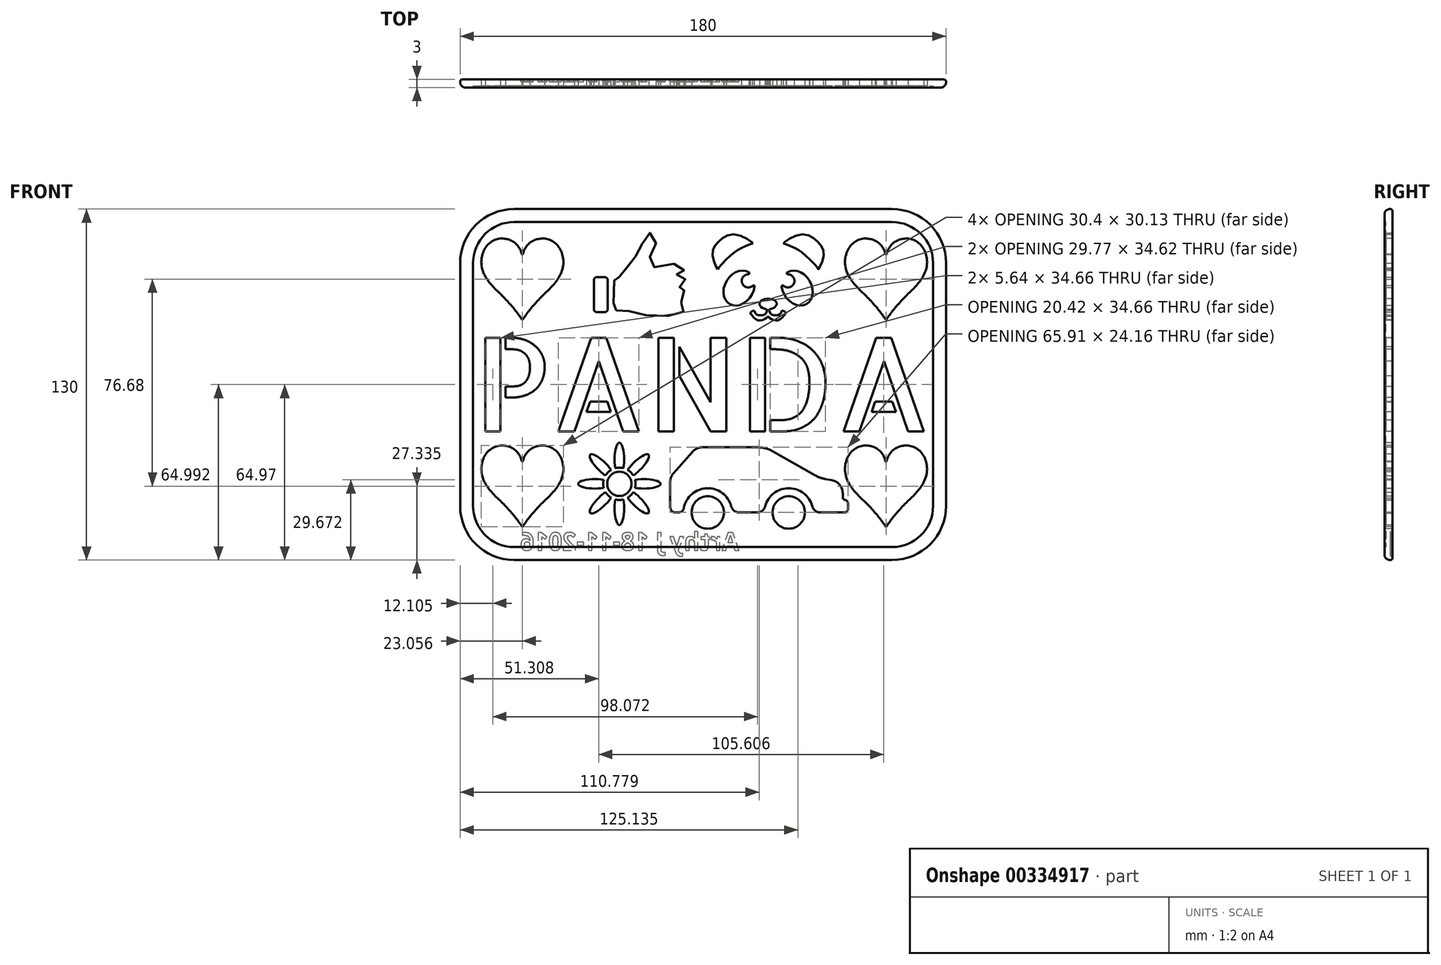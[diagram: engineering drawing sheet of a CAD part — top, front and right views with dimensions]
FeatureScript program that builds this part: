
annotation { "Feature Type Name" : "Feature", "Feature Type Description" : "" }
export const myFeature = defineFeature(function(context is Context, id is Id, definition is map)
    precondition{}
    {
        {
            var Q0;
            Q0=qCreatedBy(makeId("Front.planeOp"),FACE);
            var sketch = newSketch(context, id + "F0", { "sketchPlane" : qUnion([Q0])});
            skLineSegment(sketch, "E0.bottom", {"start": v(-90, 65) * mm, "end": v(90, 65) * mm});
            skLineSegment(sketch, "E0.top", {"start": v(-90, -65) * mm, "end": v(90, -65) * mm});
            skLineSegment(sketch, "E0.left", {"start": v(-90, 65) * mm, "end": v(-90, -65) * mm});
            skLineSegment(sketch, "E0.right", {"start": v(90, 65) * mm, "end": v(90, -65) * mm});
            skSolve(sketch);
        }
        {
            var Q0;
            Q0=qSketchRegion(id+"F0",true);
            extrude(context, id + "F1", {"entities" : qUnion([Q0]), "depth" : 3 * mm});
        }
        {
            var Q0;
            Q0=makeQuery(id+"F1.opExtrude","CAP_FACE",FACE,{"disambiguationData":[OSD([sQuery(id+"F0.wireOp",EDGE,"E0.bottom"),sQuery(id+"F0.wireOp",EDGE,"E0.top"),sQuery(id+"F0.wireOp",EDGE,"E0.left"),sQuery(id+"F0.wireOp",EDGE,"E0.right")])],"isStart":false});
            var sketch = newSketch(context, id + "F2", { "sketchPlane" : qUnion([Q0])});
            skText(sketch, "E1", { "text": "PANDA", "fontName": "AllertaStencil-Regular.ttf"});
            skText(sketch, "E2", { "text": "♥", "fontName": "NotoSansCJKjp-Regular.otf"});
            skText(sketch, "E3", { "text": "♥", "fontName": "NotoSansCJKjp-Regular.otf"});
            skText(sketch, "E4", { "text": "♥", "fontName": "NotoSansCJKjp-Regular.otf"});
            skText(sketch, "E5", { "text": "♥", "fontName": "NotoSansCJKjp-Regular.otf"});
            const initialGuessF2  = {"E1": [-0.085, -0.01734, 1, 0, 0.03468], "E2": [0.04972, 0.02534, 1, 0, 0.026], "E3": [-0.085, 0.02534, 1, 0, 0.026], "E4": [-0.085, -0.05134, 1, 0, 0.026], "E5": [0.04972, -0.05134, 1, 0, 0.026]};
            skSetInitialGuess(sketch, initialGuessF2);
            skSolve(sketch);
        }
        {
            var Q0;
            Q0=qSketchRegion(id+"F2",true);
            extrude(context, id + "F3", {"entities" : qUnion([Q0]), "operationType" : NewBodyOperationType.REMOVE, "endBound" : BoundingType.THROUGH_ALL, "oppositeDirection" : true, "depth" : 25 * mm});
        }
        {
            var Q0;
            Q0=makeQuery(id+"F1.opExtrude","SWEPT_EDGE",EDGE,{"disambiguationData":[OSD([sQuery(id+"F0.wireOp",EDGE,"E0.top"),sQuery(id+"F0.wireOp",EDGE,"E0.right")])]});
            var Q1;
            Q1=makeQuery(id+"F1.opExtrude","SWEPT_EDGE",EDGE,{"disambiguationData":[OSD([sQuery(id+"F0.wireOp",EDGE,"E0.bottom"),sQuery(id+"F0.wireOp",EDGE,"E0.right")])]});
            var Q2;
            Q2=makeQuery(id+"F1.opExtrude","SWEPT_EDGE",EDGE,{"disambiguationData":[OSD([sQuery(id+"F0.wireOp",EDGE,"E0.top"),sQuery(id+"F0.wireOp",EDGE,"E0.left")])]});
            var Q3;
            Q3=makeQuery(id+"F1.opExtrude","SWEPT_EDGE",EDGE,{"disambiguationData":[OSD([sQuery(id+"F0.wireOp",EDGE,"E0.bottom"),sQuery(id+"F0.wireOp",EDGE,"E0.left")])]});
            fillet(context, id + "F4", {"entities" : qUnion([Q0, Q1, Q2, Q3]), "radius" : 20 * mm, "tangentPropagation" : true, "allowEdgeOverflow" : false});
        }
        {
            var Q0;
            Q0=makeQuery(id+"F1.opExtrude","CAP_FACE",FACE,{"disambiguationData":[OSD([sQuery(id+"F0.wireOp",EDGE,"E0.bottom"),sQuery(id+"F0.wireOp",EDGE,"E0.top"),sQuery(id+"F0.wireOp",EDGE,"E0.left"),sQuery(id+"F0.wireOp",EDGE,"E0.right")])],"isStart":false});
            var sketch = newSketch(context, id + "F5", { "sketchPlane" : qUnion([Q0])});
            skLineSegment(sketch, "E6.0", {"start": v(-70, -60.2) * mm, "end": v(70, -60.2) * mm});
            skArc(sketch, "E6.1", {"start": v(-85.2, -45) * mm, "mid": v(-80.75, -55.75) * mm, "end": v(-70, -60.2) * mm});
            skArc(sketch, "E6.2", {"start": v(70, -60.2) * mm, "mid": v(80.75, -55.75) * mm, "end": v(85.2, -45) * mm});
            skLineSegment(sketch, "E6.3", {"start": v(-85.2, 45) * mm, "end": v(-85.2, -45) * mm});
            skLineSegment(sketch, "E6.4", {"start": v(85.2, -45) * mm, "end": v(85.2, 45) * mm});
            skArc(sketch, "E6.5", {"start": v(85.2, 45) * mm, "mid": v(80.75, 55.75) * mm, "end": v(70, 60.2) * mm});
            skLineSegment(sketch, "E6.6", {"start": v(70, 60.2) * mm, "end": v(-70, 60.2) * mm});
            skArc(sketch, "E6.7", {"start": v(-70, 60.2) * mm, "mid": v(-80.75, 55.75) * mm, "end": v(-85.2, 45) * mm});
            skSolve(sketch);
        }
        {
            var Q0;
            Q0=qSketchRegion(id+"F5",true);
            extrude(context, id + "F6", {"entities" : qUnion([Q0]), "operationType" : NewBodyOperationType.REMOVE, "oppositeDirection" : true, "depth" : 0.6 * mm});
        }
        {
            var Q0;
            Q0=makeQuery(id+"F6.boolean.opBoolean","COPY",FACE,{"derivedFrom":makeQuery(id+"F6.opExtrude","CAP_FACE",FACE,{"disambiguationData":[OSD([sQuery(id+"F5.wireOp",EDGE,"E6.0"),sQuery(id+"F5.wireOp",EDGE,"E6.1"),sQuery(id+"F5.wireOp",EDGE,"E6.2"),sQuery(id+"F5.wireOp",EDGE,"E6.3"),sQuery(id+"F5.wireOp",EDGE,"E6.4"),sQuery(id+"F5.wireOp",EDGE,"E6.5"),sQuery(id+"F5.wireOp",EDGE,"E6.6"),sQuery(id+"F5.wireOp",EDGE,"E6.7")])],"isStart":false})});
            var sketch = newSketch(context, id + "F7", { "sketchPlane" : qUnion([Q0])});
            skLineSegment(sketch, "E7", {"start": v(13.35, -47.4) * mm, "end": v(20.11, -47.4) * mm, "construction": true});
            skCircle(sketch, "E8", {"center": v(1.73, -47.4) * mm, "radius": 6 * mm});
            skCircle(sketch, "E9", {"center": v(31.73, -47.4) * mm, "radius": 6 * mm});
            skArc(sketch, "E10", {"start": v(10.45, -45.16) * mm, "mid": v(1.42, -38.41) * mm, "end": v(-7.12, -45.77) * mm});
            skArc(sketch, "E11", {"start": v(40.45, -45.16) * mm, "mid": v(31.73, -38.4) * mm, "end": v(23.02, -45.16) * mm});
            skLineSegment(sketch, "E12", {"start": v(21.73, -47.4) * mm, "end": v(11.73, -47.4) * mm});
            skLineSegment(sketch, "E13", {"start": v(-9.08, -47.4) * mm, "end": v(-10.17, -47.4) * mm});
            skLineSegment(sketch, "E14", {"start": v(-12.17, -45.4) * mm, "end": v(-12.17, -36.14) * mm});
            skLineSegment(sketch, "E15", {"start": v(-10.93, -32.84) * mm, "end": v(-4, -24.95) * mm});
            skLineSegment(sketch, "E16", {"start": v(-0.25, -23.25) * mm, "end": v(20.03, -23.25) * mm});
            skLineSegment(sketch, "E17", {"start": v(25.99, -24.83) * mm, "end": v(41.29, -33.57) * mm});
            skLineSegment(sketch, "E18", {"start": v(45.19, -34.98) * mm, "end": v(47.59, -35.4) * mm});
            skLineSegment(sketch, "E19", {"start": v(51.73, -40.32) * mm, "end": v(51.73, -41.75) * mm});
            skLineSegment(sketch, "E20", {"start": v(52.4, -42.75) * mm, "end": v(52.73, -42.75) * mm});
            skLineSegment(sketch, "E21", {"start": v(53.73, -44.07) * mm, "end": v(53.73, -46.09) * mm});
            skLineSegment(sketch, "E22", {"start": v(52.4, -47.4) * mm, "end": v(43.35, -47.4) * mm});
            skPoint(sketch, "E23.visualSharp", {"position": v(-12.17, -34.25) * mm});
            skArc(sketch, "E23.filletArc", {"start": v(-10.93, -32.84) * mm, "mid": v(-11.85, -34.37) * mm, "end": v(-12.17, -36.14) * mm});
            skPoint(sketch, "E24.visualSharp", {"position": v(-2.51, -23.25) * mm});
            skArc(sketch, "E24.filletArc", {"start": v(-0.25, -23.25) * mm, "mid": v(-2.31, -23.7) * mm, "end": v(-4, -24.95) * mm});
            skPoint(sketch, "E25.visualSharp", {"position": v(23.22, -23.25) * mm});
            skArc(sketch, "E25.filletArc", {"start": v(25.99, -24.83) * mm, "mid": v(23.11, -23.65) * mm, "end": v(20.03, -23.25) * mm});
            skPoint(sketch, "E26.visualSharp", {"position": v(43.11, -34.61) * mm});
            skArc(sketch, "E26.filletArc", {"start": v(41.29, -33.57) * mm, "mid": v(43.18, -34.44) * mm, "end": v(45.19, -34.98) * mm});
            skPoint(sketch, "E27.visualSharp", {"position": v(51.73, -36.11) * mm});
            skArc(sketch, "E27.filletArc", {"start": v(51.73, -40.32) * mm, "mid": v(50.56, -37.1) * mm, "end": v(47.59, -35.4) * mm});
            skPoint(sketch, "E28.visualSharp", {"position": v(53.73, -42.75) * mm});
            skArc(sketch, "E28.filletArc", {"start": v(53.73, -44.07) * mm, "mid": v(53.34, -43.13) * mm, "end": v(52.4, -42.75) * mm});
            skPoint(sketch, "E29.visualSharp", {"position": v(53.73, -47.4) * mm});
            skArc(sketch, "E29.filletArc", {"start": v(52.4, -47.4) * mm, "mid": v(53.34, -47.02) * mm, "end": v(53.73, -46.09) * mm});
            skPoint(sketch, "E30.visualSharp", {"position": v(51.73, -42.75) * mm});
            skArc(sketch, "E30.filletArc", {"start": v(51.73, -41.75) * mm, "mid": v(52.02, -42.45) * mm, "end": v(52.73, -42.75) * mm});
            skPoint(sketch, "E31.newPointA", {"position": v(10.73, -47.4) * mm});
            skPoint(sketch, "E31.newPointB", {"position": v(-7.31, -47.4) * mm});
            skArc(sketch, "E31.filletArc", {"start": v(10.45, -45.16) * mm, "mid": v(11.51, -46.78) * mm, "end": v(13.35, -47.4) * mm});
            skArc(sketch, "E32.filletArc", {"start": v(20.11, -47.4) * mm, "mid": v(21.95, -46.78) * mm, "end": v(23.02, -45.16) * mm});
            skPoint(sketch, "E33.visualSharp", {"position": v(40.73, -47.4) * mm});
            skArc(sketch, "E33.filletArc", {"start": v(40.45, -45.16) * mm, "mid": v(41.51, -46.78) * mm, "end": v(43.35, -47.4) * mm});
            skPoint(sketch, "E34.visualSharp", {"position": v(-7.27, -47.4) * mm});
            skArc(sketch, "E34.filletArc", {"start": v(-9.08, -47.4) * mm, "mid": v(-7.8, -46.95) * mm, "end": v(-7.12, -45.77) * mm});
            skPoint(sketch, "E35.visualSharp", {"position": v(-12.17, -47.4) * mm});
            skArc(sketch, "E35.filletArc", {"start": v(-12.17, -45.4) * mm, "mid": v(-11.59, -46.82) * mm, "end": v(-10.17, -47.4) * mm});
            skSolve(sketch);
        }
        {
            var Q0;
            Q0=qSketchRegion(id+"F7",true);
            extrude(context, id + "F8", {"entities" : qUnion([Q0]), "operationType" : NewBodyOperationType.REMOVE, "endBound" : BoundingType.THROUGH_ALL, "oppositeDirection" : true, "depth" : 25 * mm});
        }
        {
            var Q0;
            Q0=qCreatedBy(makeId("Front.planeOp"),FACE);
            var sketch = newSketch(context, id + "F9", { "sketchPlane" : qUnion([Q0])});
            skFitSpline(sketch, "E36", {"points": [v(-32.1, 27.5) * mm, v(-32.86, 27.86) * mm, v(-33.14, 28.78) * mm, v(-32.88, 38.83) * mm, v(-32.72, 39) * mm, v(-31.87, 39.13) * mm, v(-29.86, 41.3) * mm, v(-28.11, 43.43) * mm, v(-24.92, 47.62) * mm, v(-22.64, 51.97) * mm, v(-20.28, 56.13) * mm, v(-17.45, 54.28) * mm, v(-18.66, 49.2) * mm, v(-19.93, 45.57) * mm, v(-17.05, 43.26) * mm, v(-8.14, 44.72) * mm, v(-7.33, 41.85) * mm, v(-9.69, 41.12) * mm, v(-9.64, 40.61) * mm, v(-7.18, 40.03) * mm, v(-7.04, 36.55) * mm, v(-8.92, 36.07) * mm, v(-8.92, 35.64) * mm, v(-7.07, 34.9) * mm, v(-7.12, 31.5) * mm, v(-9.05, 30.54) * mm, v(-9.26, 30.08) * mm, v(-7.05, 29.74) * mm, v(-6.93, 27.4) * mm, v(-11.96, 25.52) * mm, v(-22.62, 25.9) * mm, v(-28.82, 27.45) * mm, v(-32.1, 27.5) * mm]});
            skLineSegment(sketch, "E37.bottom", {"start": v(-36.34, 39.73) * mm, "end": v(-39.43, 39.73) * mm});
            skLineSegment(sketch, "E37.top", {"start": v(-36.34, 26.85) * mm, "end": v(-39.43, 26.85) * mm});
            skLineSegment(sketch, "E37.left", {"start": v(-35.34, 38.73) * mm, "end": v(-35.34, 27.85) * mm});
            skLineSegment(sketch, "E37.right", {"start": v(-40.43, 38.73) * mm, "end": v(-40.43, 27.85) * mm});
            skPoint(sketch, "E38.visualSharp", {"position": v(-35.34, 39.73) * mm});
            skArc(sketch, "E38.filletArc", {"start": v(-35.34, 38.73) * mm, "mid": v(-35.63, 39.44) * mm, "end": v(-36.34, 39.73) * mm});
            skPoint(sketch, "E39.visualSharp", {"position": v(-40.43, 39.73) * mm});
            skArc(sketch, "E39.filletArc", {"start": v(-39.43, 39.73) * mm, "mid": v(-40.14, 39.44) * mm, "end": v(-40.43, 38.73) * mm});
            skPoint(sketch, "E40.visualSharp", {"position": v(-40.43, 26.85) * mm});
            skArc(sketch, "E40.filletArc", {"start": v(-40.43, 27.85) * mm, "mid": v(-40.14, 27.15) * mm, "end": v(-39.43, 26.85) * mm});
            skPoint(sketch, "E41.visualSharp", {"position": v(-35.34, 26.85) * mm});
            skArc(sketch, "E41.filletArc", {"start": v(-36.34, 26.85) * mm, "mid": v(-35.63, 27.15) * mm, "end": v(-35.34, 27.85) * mm});
            skSolve(sketch);
        }
        {
            var Q0;
            Q0 = qSketchRegion(id + "F9", true);
            extrude(context, id + "F10", {"entities" : qUnion([Q0]), "operationType" : NewBodyOperationType.REMOVE, "depth" : 25 * mm});
        }
        {
            var Q0;
            Q0=qCreatedBy(makeId("Front.planeOp"),FACE);
            var sketch = newSketch(context, id + "F11", { "sketchPlane" : qUnion([Q0])});
            skFitSpline(sketch, "E42", {"points": [v(5.47, 42.75) * mm, v(3.5, 47.69) * mm, v(5.55, 52.74) * mm, v(11.99, 55.63) * mm, v(18.34, 52.29) * mm, v(17.82, 52.06) * mm, v(13.7, 50.34) * mm, v(10.3, 47.94) * mm, v(5.7, 43.07) * mm, v(5.47, 42.75) * mm]});
            skLineSegment(sketch, "E43", {"start": v(24.08, 21.55) * mm, "end": v(24.08, 60.73) * mm, "construction": true});
            skEllipticalArc(sketch, "E44", {});
            skArc(sketch, "E45", {"start": v(16.74, 40.84) * mm, "mid": v(14.48, 37.5) * mm, "end": v(18.4, 36.61) * mm});
            skEllipticalArc(sketch, "E46", {});
            skFitSpline(sketch, "E47", {"points": [v(23.53, 27.98) * mm, v(23.63, 27.33) * mm, v(23, 26.13) * mm, v(21.04, 25.62) * mm, v(19.33, 26.41) * mm, v(18.83, 27.35) * mm, v(17.54, 26.58) * mm, v(17.7, 26.17) * mm, v(19.7, 24.06) * mm, v(22.33, 23.97) * mm, v(24.08, 25.26) * mm], "startDerivative": vector(2.78, -9.13) * mm, "endDerivative": vector(13.23, 12.72) * mm});
            skEllipticalArc(sketch, "E48.MirrorC", {});
            skArc(sketch, "E49.MirrorC", {"start": v(31.42, 40.84) * mm, "mid": v(33.68, 37.5) * mm, "end": v(29.76, 36.61) * mm});
            skFitSpline(sketch, "E50.MirrorCS", {"points": [v(24.64, 27.98) * mm, v(24.54, 27.33) * mm, v(25.16, 26.13) * mm, v(27.13, 25.62) * mm, v(28.83, 26.41) * mm, v(29.33, 27.35) * mm, v(30.63, 26.58) * mm, v(30.46, 26.17) * mm, v(28.47, 24.06) * mm, v(25.83, 23.97) * mm, v(24.08, 25.26) * mm], "startDerivative": vector(-2.78, -9.13) * mm, "endDerivative": vector(-13.23, 12.72) * mm});
            skFitSpline(sketch, "E51.MirrorC", {"points": [v(42.7, 42.75) * mm, v(44.66, 47.69) * mm, v(42.61, 52.74) * mm, v(36.18, 55.63) * mm, v(29.83, 52.29) * mm, v(30.34, 52.06) * mm, v(34.47, 50.34) * mm, v(37.86, 47.94) * mm, v(42.47, 43.07) * mm, v(42.7, 42.75) * mm]});
            skPoint(sketch, "E52.visualSharp", {"position": v(29.93, 40.33) * mm});
            skArc(sketch, "E52.filletArc", {"start": v(31.21, 41.57) * mm, "mid": v(31.04, 41.13) * mm, "end": v(31.42, 40.84) * mm});
            skPoint(sketch, "E53.visualSharp", {"position": v(29.06, 37.78) * mm});
            skArc(sketch, "E53.filletArc", {"start": v(29.76, 36.61) * mm, "mid": v(29.3, 36.68) * mm, "end": v(29.1, 36.27) * mm});
            skPoint(sketch, "E54.visualSharp", {"position": v(18.23, 40.33) * mm});
            skArc(sketch, "E54.filletArc", {"start": v(16.74, 40.84) * mm, "mid": v(17.12, 41.13) * mm, "end": v(16.95, 41.57) * mm});
            skPoint(sketch, "E55.visualSharp", {"position": v(19.1, 37.78) * mm});
            skArc(sketch, "E55.filletArc", {"start": v(19.07, 36.27) * mm, "mid": v(18.86, 36.68) * mm, "end": v(18.4, 36.61) * mm});
            const initialGuessF11  = {"E44": [0.013339819386601448, 0.03574172034859657, 0.5229127185200972, 0.8523862321799441, 0.006860580511075327, 0.0053319260220896555, 6.277866607995079, 5.238855889684281], "E46": [0.024082258343696594, 0.02989092841744423, 1, 0, 0.003207892982778297, 0.0019368553525155674, 4.885729797338385, 4.539048163430994], "E48.MirrorC": [0.03482469730079174, 0.03574172034859657, -0.5229127185200972, 0.8523862321799441, 0.006860580511075327, 0.0053319260220896555, 1.0443294174953037, 0.005318699184505012]};
            skSetInitialGuess(sketch, initialGuessF11);
            skSolve(sketch);
        }
        {
            var Q0;
            Q0 = qSketchRegion(id + "F11", true);
            extrude(context, id + "F12", {"entities" : qUnion([Q0]), "operationType" : NewBodyOperationType.REMOVE, "depth" : 25 * mm});
        }
        {
            var Q0;
            Q0=qCreatedBy(makeId("Front.planeOp"),FACE);
            var sketch = newSketch(context, id + "F13", { "sketchPlane" : qUnion([Q0])});
            skCircle(sketch, "E56", {"center": v(-31, -36.79) * mm, "radius": 4.5 * mm});
            skArc(sketch, "E57", {"start": v(-25.2, -38.29) * mm, "mid": v(-25, -36.79) * mm, "end": v(-25.2, -35.29) * mm});
            skLineSegment(sketch, "E58", {"start": v(-31, -36.79) * mm, "end": v(-15.26, -36.79) * mm, "construction": true});
            skEllipticalArc(sketch, "E59", {});
            skEllipticalArc(sketch, "E60.1.0", {});
            skArc(sketch, "E60.1.1", {"start": v(-25.83, -33.74) * mm, "mid": v(-26.76, -32.54) * mm, "end": v(-27.95, -31.62) * mm});
            skEllipticalArc(sketch, "E60.2.0", {});
            skArc(sketch, "E60.2.1", {"start": v(-29.5, -30.98) * mm, "mid": v(-31, -30.79) * mm, "end": v(-32.5, -30.98) * mm});
            skEllipticalArc(sketch, "E60.3.0", {});
            skArc(sketch, "E60.3.1", {"start": v(-34.05, -31.62) * mm, "mid": v(-35.24, -32.54) * mm, "end": v(-36.17, -33.74) * mm});
            skEllipticalArc(sketch, "E60.4.0", {});
            skArc(sketch, "E60.4.1", {"start": v(-36.8, -35.29) * mm, "mid": v(-37, -36.79) * mm, "end": v(-36.8, -38.29) * mm});
            skEllipticalArc(sketch, "E60.5.0", {});
            skArc(sketch, "E60.5.1", {"start": v(-36.17, -39.83) * mm, "mid": v(-35.24, -41.03) * mm, "end": v(-34.05, -41.96) * mm});
            skEllipticalArc(sketch, "E60.6.0", {});
            skArc(sketch, "E60.6.1", {"start": v(-32.5, -42.6) * mm, "mid": v(-31, -42.79) * mm, "end": v(-29.5, -42.6) * mm});
            skEllipticalArc(sketch, "E60.7.0", {});
            skArc(sketch, "E60.7.1", {"start": v(-27.95, -41.96) * mm, "mid": v(-26.76, -41.03) * mm, "end": v(-25.83, -39.83) * mm});
            const initialGuessF13  = {"E59": [-0.021932768562383655, -0.036786943674087524, 1, 0, 0.006194742366557021, 0.0017635600769210448, 4.158627190019384, 2.1245581171602024], "E60.1.0": [-0.02458849916387363, -0.03037544283796116, 0.7071067811865476, 0.7071067811865475, 0.006194742366557021, 0.0017635600769210448, 4.158627190019384, 2.124558117160202], "E60.2.0": [-0.031, -0.02771971223647118, 0, 1, 0.006194742366557021, 0.0017635600769210448, 4.158627190019384, 2.124558117160202], "E60.3.0": [-0.03741150083612636, -0.030375442837961154, -0.7071067811865475, 0.7071067811865476, 0.006194742366557021, 0.0017635600769210448, 4.158627190019384, 2.124558117160202], "E60.4.0": [-0.04006723143761634, -0.036786943674087524, -1, 0, 0.006194742366557021, 0.0017635600769210448, 4.158627190019384, 2.124558117160202], "E60.5.0": [-0.03741150083612637, -0.04319844451021389, -0.7071067811865477, -0.7071067811865475, 0.006194742366557021, 0.0017635600769210448, 4.158627190019384, 2.124558117160202], "E60.6.0": [-0.031, -0.045854175111703865, 0, -1, 0.006194742366557021, 0.0017635600769210448, 4.158627190019384, 2.124558117160202], "E60.7.0": [-0.024588499163873637, -0.04319844451021389, 0.7071067811865474, -0.7071067811865477, 0.006194742366557021, 0.0017635600769210448, 4.158627190019384, 2.124558117160202]};
            skSetInitialGuess(sketch, initialGuessF13);
            skSolve(sketch);
        }
        {
            var Q0;
            Q0 = qSketchRegion(id + "F13", true);
            extrude(context, id + "F14", {"entities" : qUnion([Q0]), "operationType" : NewBodyOperationType.REMOVE, "depth" : 25 * mm});
        }
        {
            var Q0;
            Q0=makeQuery(id+"F6.boolean.opBoolean","COPY",EDGE,{"derivedFrom":makeQuery(id+"F6.opExtrude","CAP_EDGE",EDGE,{"disambiguationData":[OSD([sQuery(id+"F5.wireOp",EDGE,"E6.3")])],"isStart":true})});
            var Q1;
            Q1=makeQuery(id+"F1.opExtrude","CAP_EDGE",EDGE,{"disambiguationData":[OSD([sQuery(id+"F0.wireOp",EDGE,"E0.left")])],"isStart":false});
            fillet(context, id + "F15", {"entities" : qUnion([Q0, Q1]), "radius" : 2 * mm, "tangentPropagation" : true, "allowEdgeOverflow" : false});
        }
        {
            var Q0;
            Q0=makeQuery(id+"F1.opExtrude","CAP_EDGE",EDGE,{"disambiguationData":[OSD([sQuery(id+"F0.wireOp",EDGE,"E0.right")])],"isStart":true});
            fillet(context, id + "F16", {"entities" : qUnion([Q0]), "radius" : 0.8 * mm, "tangentPropagation" : true, "allowEdgeOverflow" : false});
        }
        {
            var Q0;
            {var subQ0=sQuery(id+"F0.wireOp",EDGE,"E0.right");var subQ1=sQuery(id+"F0.wireOp",EDGE,"E0.bottom");var subQ2=makeQuery(id+"F1.opExtrude","CAP_FACE",FACE,{"disambiguationData":[OSD([subQ1,sQuery(id+"F0.wireOp",EDGE,"E0.top"),sQuery(id+"F0.wireOp",EDGE,"E0.left"),subQ0])],"isStart":true});Q0=makeQuery(id+"F16.opFillet","BLEND_VERTEX",VERTEX,{"blendedFrom":[makeQuery(id+"F4.opFillet","BLEND_EDGE",EDGE,{"blendedFrom":[makeQuery(id+"F1.opExtrude","SWEPT_EDGE",EDGE,{"disambiguationData":[OSD([subQ1,subQ0])]}),subQ2],"blendedInto":[subQ2]}),makeQuery(id+"F1.opExtrude","CAP_EDGE",EDGE,{"disambiguationData":[OSD([subQ1])],"isStart":true}),subQ2],"blendedInto":[subQ2]});}
            var Q1;
            {var subQ0=sQuery(id+"F0.wireOp",EDGE,"E0.left");var subQ1=sQuery(id+"F0.wireOp",EDGE,"E0.bottom");var subQ2=makeQuery(id+"F1.opExtrude","CAP_FACE",FACE,{"disambiguationData":[OSD([subQ1,sQuery(id+"F0.wireOp",EDGE,"E0.top"),subQ0,sQuery(id+"F0.wireOp",EDGE,"E0.right")])],"isStart":true});Q1=makeQuery(id+"F16.opFillet","BLEND_VERTEX",VERTEX,{"blendedFrom":[makeQuery(id+"F4.opFillet","BLEND_EDGE",EDGE,{"blendedFrom":[makeQuery(id+"F1.opExtrude","SWEPT_EDGE",EDGE,{"disambiguationData":[OSD([subQ1,subQ0])]}),subQ2],"blendedInto":[subQ2]}),makeQuery(id+"F1.opExtrude","CAP_EDGE",EDGE,{"disambiguationData":[OSD([subQ1])],"isStart":true}),subQ2],"blendedInto":[subQ2]});}
            var Q2;
            {var subQ0=sQuery(id+"F0.wireOp",EDGE,"E0.right");var subQ1=sQuery(id+"F0.wireOp",EDGE,"E0.top");var subQ2=makeQuery(id+"F1.opExtrude","CAP_FACE",FACE,{"disambiguationData":[OSD([sQuery(id+"F0.wireOp",EDGE,"E0.bottom"),subQ1,sQuery(id+"F0.wireOp",EDGE,"E0.left"),subQ0])],"isStart":true});Q2=makeQuery(id+"F16.opFillet","BLEND_VERTEX",VERTEX,{"blendedFrom":[makeQuery(id+"F4.opFillet","BLEND_EDGE",EDGE,{"blendedFrom":[makeQuery(id+"F1.opExtrude","SWEPT_EDGE",EDGE,{"disambiguationData":[OSD([subQ1,subQ0])]}),subQ2],"blendedInto":[subQ2]}),makeQuery(id+"F1.opExtrude","CAP_EDGE",EDGE,{"disambiguationData":[OSD([subQ1])],"isStart":true}),subQ2],"blendedInto":[subQ2]});}
            cPlane(context, id + "F17", {"entities" : qUnion([Q0, Q1, Q2]), "cplaneType" : CPlaneType.THREE_POINT, "offset" : 25 * mm, "width" : 150 * mm, "height" : 150 * mm});
        }
        {
            var Q0;
            Q0=qCreatedBy(id+"F17.planeOp",FACE);
            var sketch = newSketch(context, id + "F18", { "sketchPlane" : qUnion([Q0])});
            skText(sketch, "E61", { "text": "Arthy J 18-11-2016", "fontName": "OpenSans-Bold.ttf"});
            const initialGuessF18  = {"E61": [-0.01327, -0.0614, 1, 0, 0.00658]};
            skSetInitialGuess(sketch, initialGuessF18);
            skSolve(sketch);
        }
        {
            var Q0;
            Q0 = qSketchRegion(id + "F18", true);
            extrude(context, id + "F19", {"entities" : qUnion([Q0]), "operationType" : NewBodyOperationType.REMOVE, "oppositeDirection" : true, "depth" : 0.8 * mm});
        }
    });
